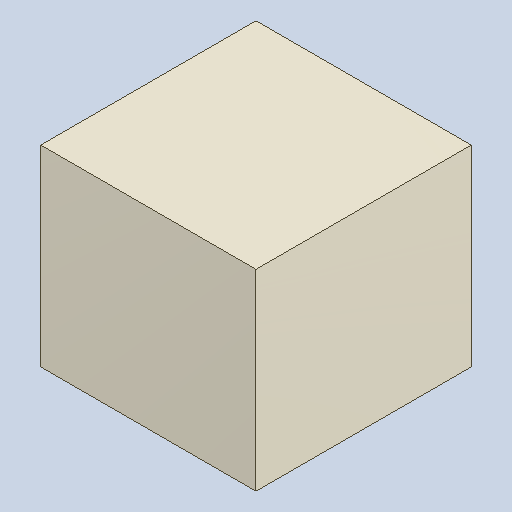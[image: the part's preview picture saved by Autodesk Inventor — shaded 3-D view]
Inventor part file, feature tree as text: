
AUTODESK INVENTOR PART (.ipt)
format: ipt  version: 2023.4 (Build 274418000, 418)  size: 81,920 bytes
history: native  units: mm
features: extrude x1
ambient origin geometry x8: Origin, YZ Plane, XZ Plane, XY Plane, X Axis, Y Axis, Z Axis, Center Point
bodies: Solid1 (feature_tree)
feature tree (1):
  extrude  "Extruded_2"  [1 undecoded]
note: 1 required parameter value undecoded (feature->parameter linkage not recoverable at this tier; creation-order binding heuristic only, values carry confidence <= 0.55)
